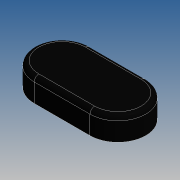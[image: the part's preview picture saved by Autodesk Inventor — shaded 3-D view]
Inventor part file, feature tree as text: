
AUTODESK INVENTOR PART (.ipt)
format: ipt  version: 2019 (Build 230136000, 136)  size: 220,672 bytes
history: native  units: mm
features: extrude x1, fillet x1, mirror x1, sketch x1
ambient origin geometry x8: Origin, YZ Plane, XZ Plane, XY Plane, X Axis, Y Axis, Z Axis, Center Point
bodies: Solid1 (feature_tree)
feature tree (4):
  extrude  "Extrusion1"  Depth=6.0mm
  fillet  "Fillet1"  Radius=5.0mm
  mirror  "Mirror1"
  sketch  "Sketch1"  dims[d0=12.0mm d1=6.0mm d2=5.0mm d3=0.0mm d4=1.0mm]
